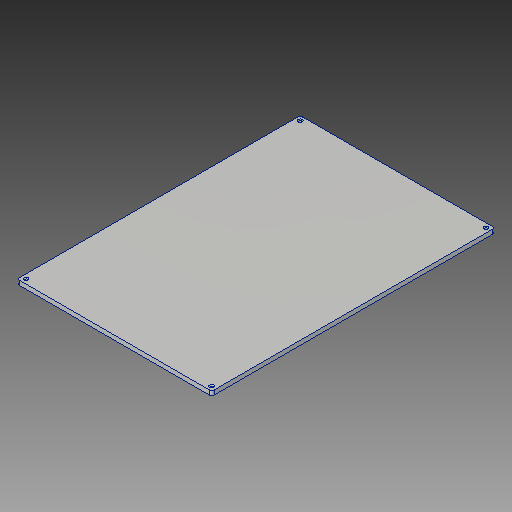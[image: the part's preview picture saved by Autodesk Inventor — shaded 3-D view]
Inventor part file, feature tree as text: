
AUTODESK INVENTOR PART (.ipt)
format: ipt  version: 2019 (Build 230136000, 136)  size: 146,432 bytes
history: native  units: mm
features: sketch x2, other x2, sheet_metal_op x1, fillet x1, hole x1
ambient origin geometry x8: Origin, YZ Plane, XZ Plane, XY Plane, X Axis, Y Axis, Z Axis, Center Point
bodies: Solid1 (feature_tree)
feature tree (7):
  sheet_metal_op  "Face1"
  fillet  "Fillet1"  Radius=220.0mm
  hole  "Hole1"  [1 undecoded]
  sketch  "Sketch1"  dims[d1=320.0mm d2=0.8mm]
  other  "Plate1"
  sketch  "Sketch2"  dims[d3=3.0mm d4=310.0mm d5=210.0mm d6=3.2mm d9=3.0mm d10=6.0mm d11=5.0mm d12=2.0mm d13=90.0deg d14=8.8mm d15=0.0mm d16=5.0mm]
  other  "Definition1"
note: 1 required parameter value undecoded (feature->parameter linkage not recoverable at this tier; creation-order binding heuristic only, values carry confidence <= 0.55)
